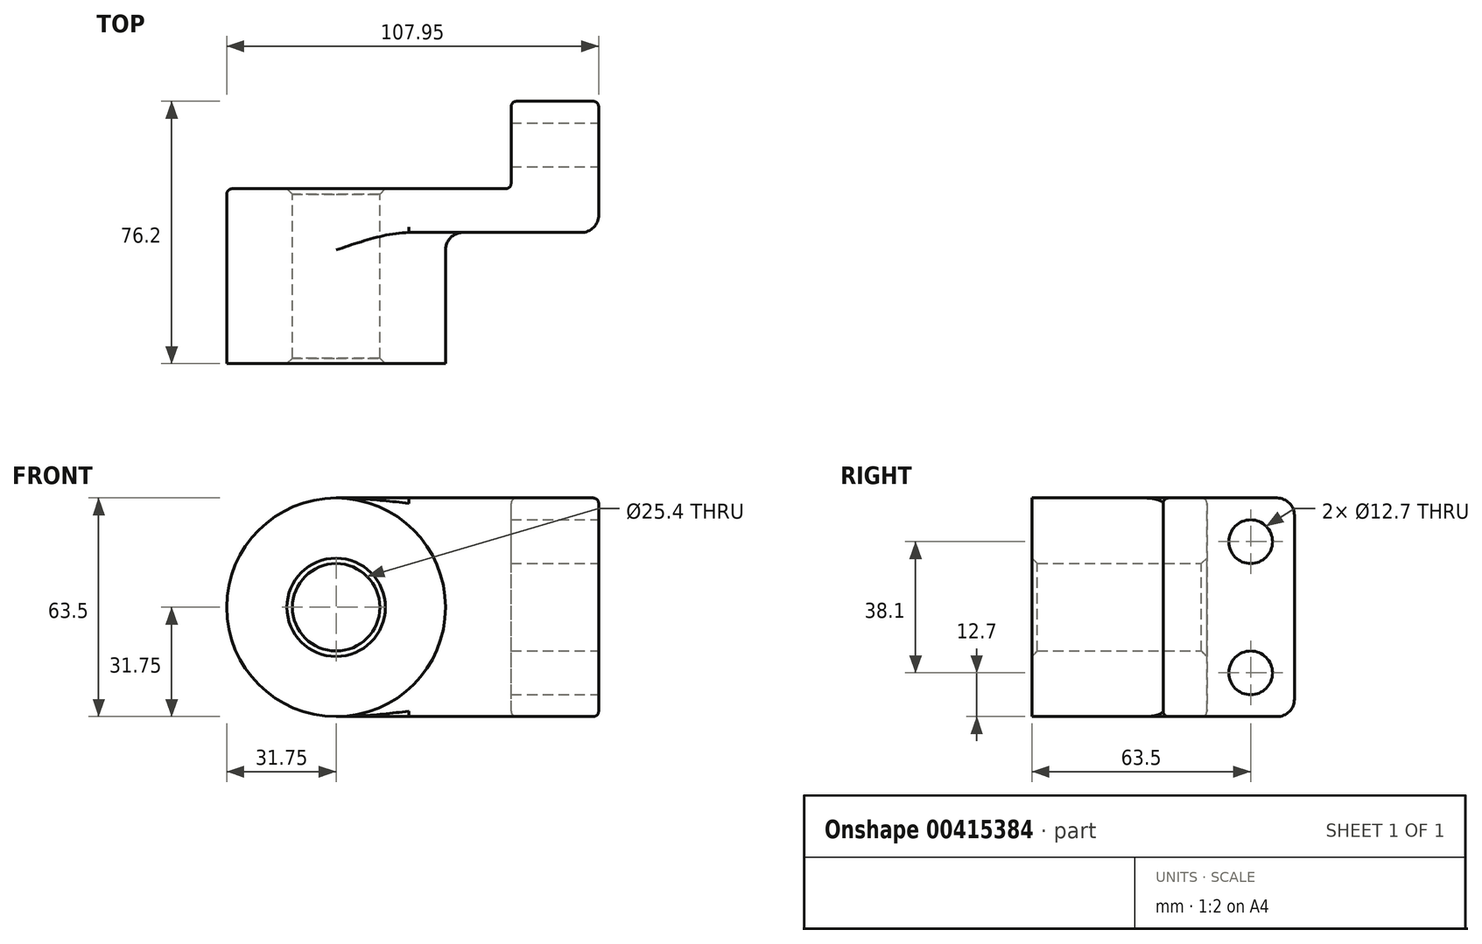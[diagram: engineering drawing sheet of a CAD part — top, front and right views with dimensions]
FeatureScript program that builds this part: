
annotation { "Feature Type Name" : "Feature", "Feature Type Description" : "" }
export const myFeature = defineFeature(function(context is Context, id is Id, definition is map)
    precondition{}
    {
        {
            var Q0;
            Q0=qCreatedBy(makeId("Front.planeOp"),FACE);
            var sketch = newSketch(context, id + "F0", { "sketchPlane" : qUnion([Q0])});
            skLineSegment(sketch, "E0.bottom", {"start": v(38.1, 31.75) * mm, "end": v(-38.1, 31.75) * mm});
            skLineSegment(sketch, "E0.top", {"start": v(38.1, -31.75) * mm, "end": v(-38.1, -31.75) * mm});
            skLineSegment(sketch, "E0.left", {"start": v(38.1, 31.75) * mm, "end": v(38.1, -31.75) * mm});
            skLineSegment(sketch, "E0.right", {"start": v(-38.1, 31.75) * mm, "end": v(-38.1, -31.75) * mm});
            skPoint(sketch, "E0.middle", {"position": v(0, 0) * mm});
            skCircle(sketch, "E1", {"center": v(-38.1, 0) * mm, "radius": 31.75 * mm});
            skCircle(sketch, "E2", {"center": v(-38.1, 0) * mm, "radius": 12.7 * mm});
            skSolve(sketch);
        }
        {
            var Q0;
            Q0 = qSketchRegion(id + "F0", true);
            extrude(context, id + "F1", {"entities" : qUnion([Q0]), "depth" : 12.7 * mm});
        }
        {
            var Q0;
            {var subQ1=sQuery(id+"F0.wireOp",EDGE,"E0.right");var subQ3=sQuery(id+"F0.wireOp",EDGE,"E2");var subQ4=makeQuery(id+"F0.imprint","INTERSECT",VERTEX,{"disambiguationData":[OD(0.0)],"derivedFrom":[subQ1,subQ3]});Q0=makeQuery(id+"F0.imprint","IMPRINT",FACE,{"disambiguationData":[TD([[makeQuery(id+"F0.imprint","IMPRINT",EDGE,{"disambiguationData":[TD([[subQ4,-1.0]])],"derivedFrom":subQ3}),-1.0]])]});}
            var Q1;
            {var subQ1=sQuery(id+"F0.wireOp",EDGE,"E0.right");var subQ3=sQuery(id+"F0.wireOp",EDGE,"E2");var subQ4=makeQuery(id+"F0.imprint","INTERSECT",VERTEX,{"disambiguationData":[OD(0.0)],"derivedFrom":[subQ1,subQ3]});Q1=makeQuery(id+"F0.imprint","IMPRINT",FACE,{"disambiguationData":[TD([[makeQuery(id+"F0.imprint","IMPRINT",EDGE,{"disambiguationData":[TD([[subQ4,1.0]])],"derivedFrom":subQ3}),-1.0]])]});}
            extrude(context, id + "F2", {"entities" : qUnion([Q0, Q1]), "operationType" : NewBodyOperationType.ADD, "depth" : 50.8 * mm});
        }
        {
            var Q0;
            Q0=makeQuery(id+"F1.opExtrude","SWEPT_FACE",FACE,{"disambiguationData":[OSD([sQuery(id+"F0.wireOp",EDGE,"E0.left")])]});
            var sketch = newSketch(context, id + "F3", { "sketchPlane" : qUnion([Q0])});
            skLineSegment(sketch, "E3.bottom", {"start": v(-12.7, -31.75) * mm, "end": v(25.4, -31.75) * mm});
            skLineSegment(sketch, "E3.top", {"start": v(-12.7, 31.75) * mm, "end": v(25.4, 31.75) * mm});
            skLineSegment(sketch, "E3.left", {"start": v(-12.7, -31.75) * mm, "end": v(-12.7, 31.75) * mm});
            skLineSegment(sketch, "E3.right", {"start": v(25.4, -31.75) * mm, "end": v(25.4, 31.75) * mm});
            skCircle(sketch, "E4", {"center": v(12.7, -19.05) * mm, "radius": 6.35 * mm});
            skLineSegment(sketch, "E5", {"start": v(0, 0) * mm, "end": v(25.4, 0) * mm, "construction": true});
            skCircle(sketch, "E6.MirrorC", {"center": v(12.7, 19.05) * mm, "radius": 6.35 * mm});
            skSolve(sketch);
        }
        {
            var Q0;
            Q0 = qSketchRegion(id + "F3", true);
            extrude(context, id + "F4", {"entities" : qUnion([Q0]), "operationType" : NewBodyOperationType.ADD, "oppositeDirection" : true, "depth" : 25.4 * mm});
        }
        {
            var Q0;
            {var subQ0=sQuery(id+"F0.wireOp",EDGE,"E1");Q0=makeQuery(id+"F2.boolean.opBoolean","INTERSECT",EDGE,{"derivedFrom":[makeQuery(id+"F1.opExtrude","CAP_FACE",FACE,{"disambiguationData":[OSD([sQuery(id+"F0.wireOp",EDGE,"E0.bottom"),sQuery(id+"F0.wireOp",EDGE,"E0.top"),sQuery(id+"F0.wireOp",EDGE,"E0.left"),subQ0,sQuery(id+"F0.wireOp",EDGE,"E2")])],"isStart":false}),makeQuery(id+"F2.opExtrude","SWEPT_FACE",FACE,{"disambiguationData":[OSD([subQ0])]})]});}
            var Q1;
            Q1=makeQuery(id+"F1.opExtrude","CAP_EDGE",EDGE,{"disambiguationData":[OSD([sQuery(id+"F0.wireOp",EDGE,"E0.left")])],"isStart":false});
            var Q2;
            Q2=makeQuery(id+"F4.opExtrude","SWEPT_EDGE",EDGE,{"disambiguationData":[OSD([sQuery(id+"F3.wireOp",EDGE,"E3.bottom"),sQuery(id+"F3.wireOp",EDGE,"E3.right")])]});
            var Q3;
            Q3=makeQuery(id+"F4.opExtrude","SWEPT_EDGE",EDGE,{"disambiguationData":[OSD([sQuery(id+"F3.wireOp",EDGE,"E3.top"),sQuery(id+"F3.wireOp",EDGE,"E3.right")])]});
            fillet(context, id + "F5", {"entities" : qUnion([Q0, Q1, Q2, Q3]), "radius" : 5.08 * mm, "tangentPropagation" : true, "allowEdgeOverflow" : false});
        }
        {
            var Q0;
            Q0=makeQuery(id+"F1.opExtrude","CAP_EDGE",EDGE,{"disambiguationData":[OSD([sQuery(id+"F0.wireOp",EDGE,"E0.top")])],"isStart":false});
            var Q1;
            Q1=makeQuery(id+"F1.opExtrude","CAP_EDGE",EDGE,{"disambiguationData":[OSD([sQuery(id+"F0.wireOp",EDGE,"E0.top")])],"isStart":true});
            var Q2;
            Q2=makeQuery(id+"F4.opExtrude","CAP_EDGE",EDGE,{"disambiguationData":[OSD([sQuery(id+"F3.wireOp",EDGE,"E3.bottom")])],"isStart":false});
            var Q3;
            Q3=makeQuery(id+"F4.boolean.opBoolean","INTERSECT",EDGE,{"derivedFrom":[makeQuery(id+"F1.opExtrude","CAP_FACE",FACE,{"disambiguationData":[OSD([sQuery(id+"F0.wireOp",EDGE,"E0.bottom"),sQuery(id+"F0.wireOp",EDGE,"E0.top"),sQuery(id+"F0.wireOp",EDGE,"E0.left"),sQuery(id+"F0.wireOp",EDGE,"E1"),sQuery(id+"F0.wireOp",EDGE,"E2")])],"isStart":true}),makeQuery(id+"F4.opExtrude","CAP_FACE",FACE,{"disambiguationData":[OSD([sQuery(id+"F3.wireOp",EDGE,"E3.bottom"),sQuery(id+"F3.wireOp",EDGE,"E3.top"),sQuery(id+"F3.wireOp",EDGE,"E3.left"),sQuery(id+"F3.wireOp",EDGE,"E3.right"),sQuery(id+"F3.wireOp",EDGE,"E4"),sQuery(id+"F3.wireOp",EDGE,"E6.MirrorC")])],"isStart":false})]});
            fillet(context, id + "F6", {"entities" : qUnion([Q0, Q1, Q2, Q3]), "radius" : 1.59 * mm, "tangentPropagation" : true, "allowEdgeOverflow" : false});
        }
        {
            var Q0;
            Q0=makeQuery(id+"F2.opExtrude","CAP_EDGE",EDGE,{"disambiguationData":[OSD([sQuery(id+"F0.wireOp",EDGE,"E2")])],"isStart":false});
            var Q1;
            Q1=makeQuery(id+"F1.opExtrude","CAP_EDGE",EDGE,{"disambiguationData":[OSD([sQuery(id+"F0.wireOp",EDGE,"E2")])],"isStart":true});
            chamfer(context, id + "F7", {"entities" : qUnion([Q0, Q1]), "width" : 1.59 * mm, "tangentPropagation" : true});
        }
    });
